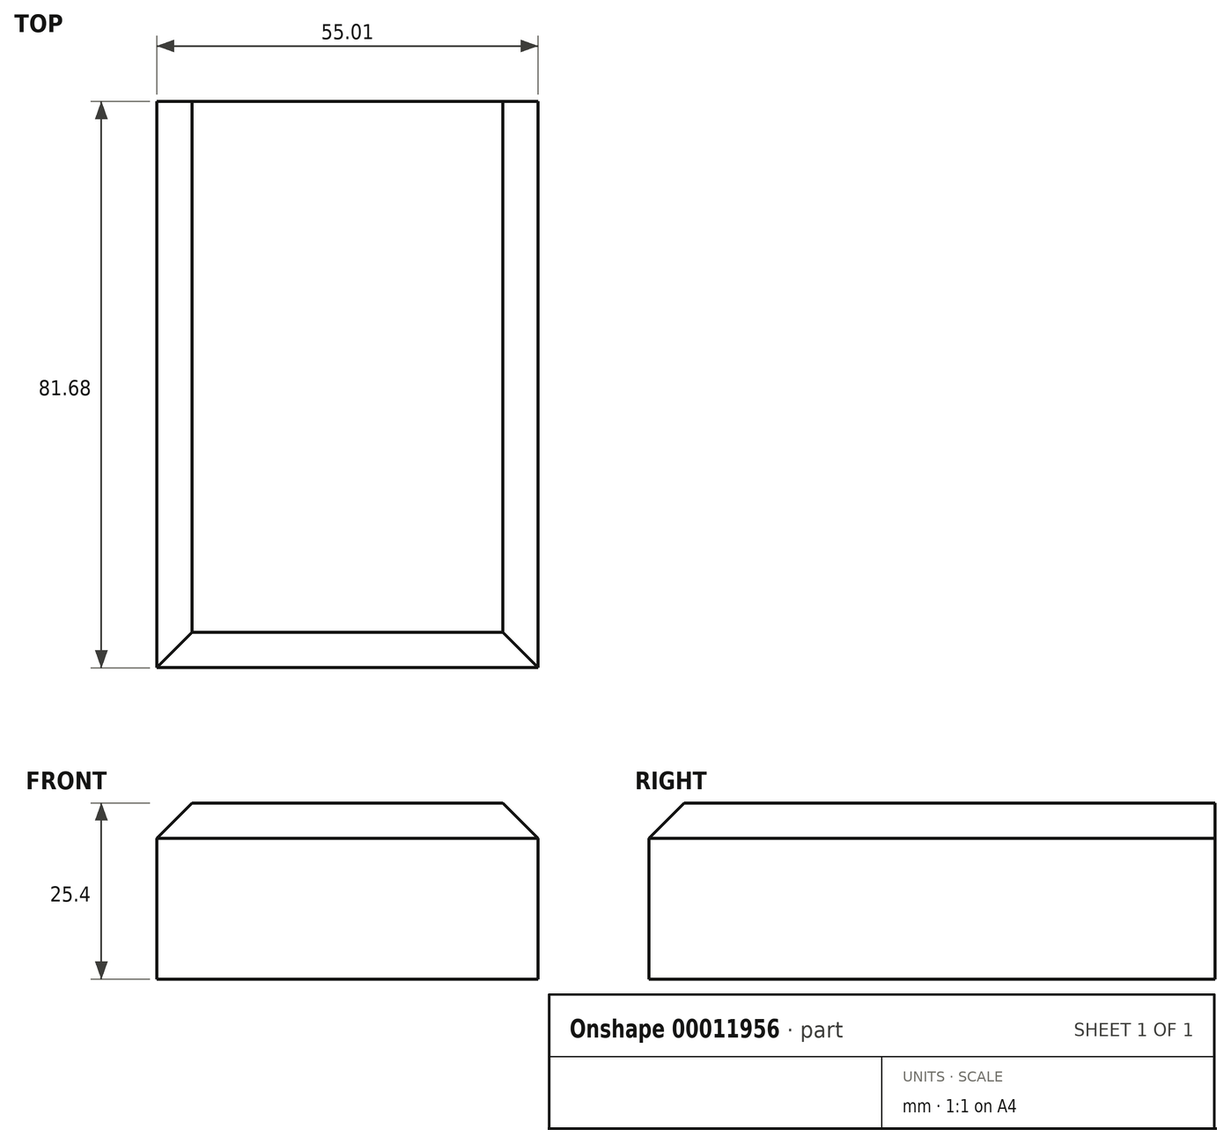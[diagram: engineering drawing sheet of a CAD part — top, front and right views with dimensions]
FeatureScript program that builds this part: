
annotation { "Feature Type Name" : "Feature", "Feature Type Description" : "" }
export const myFeature = defineFeature(function(context is Context, id is Id, definition is map)
    precondition{}
    {
        {
            var Q0;
            Q0=qCreatedBy(makeId("Top.planeOp"),FACE);
            var sketch = newSketch(context, id + "F0", { "sketchPlane" : qUnion([Q0])});
            skLineSegment(sketch, "E0.bottom", {"start": v(-38.06, -43.62) * mm, "end": v(16.95, -43.62) * mm});
            skLineSegment(sketch, "E0.top", {"start": v(-38.06, 38.06) * mm, "end": v(16.95, 38.06) * mm});
            skLineSegment(sketch, "E0.left", {"start": v(-38.06, -43.62) * mm, "end": v(-38.06, 38.06) * mm});
            skLineSegment(sketch, "E0.right", {"start": v(16.95, -43.62) * mm, "end": v(16.95, 38.06) * mm});
            skSolve(sketch);
        }
        {
            var Q0;
            Q0 = qSketchRegion(id + "F0", true);
            extrude(context, id + "F1", {"entities" : qUnion([Q0]), "depth" : 25.4 * mm});
        }
        {
            var Q0;
            Q0=makeQuery(id+"F1.opExtrude","CAP_EDGE",EDGE,{"disambiguationData":[OSD([sQuery(id+"F0.wireOp",EDGE,"E0.bottom")])],"isStart":false});
            var Q1;
            Q1=makeQuery(id+"F1.opExtrude","CAP_EDGE",EDGE,{"disambiguationData":[OSD([sQuery(id+"F0.wireOp",EDGE,"E0.right")])],"isStart":false});
            var Q2;
            Q2=makeQuery(id+"F1.opExtrude","CAP_EDGE",EDGE,{"disambiguationData":[OSD([sQuery(id+"F0.wireOp",EDGE,"E0.left")])],"isStart":false});
            chamfer(context, id + "F2", {"entities" : qUnion([Q0, Q1, Q2]), "width" : 5.08 * mm, "tangentPropagation" : true});
        }
    });
